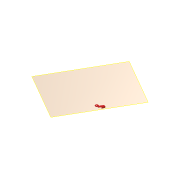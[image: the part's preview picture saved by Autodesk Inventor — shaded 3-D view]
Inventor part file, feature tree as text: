
AUTODESK INVENTOR PART (.ipt)
format: ipt  version: 2016 (Build 200138000, 138)  size: 402,432 bytes
history: native  units: mm
features: sheet_metal_op x13, reference x9, sketch x8, other x6, fillet x5, extrude x2, projected_geometry x2, plane x1
ambient origin geometry x8: Origin, YZ Plane, XZ Plane, XY Plane, X Axis, Y Axis, Z Axis, Center Point
bodies: Solid1 (feature_tree)
feature tree (46):
  plane  "Work Plane1"
  sheet_metal_op  "Face1"
  extrude  "Extrusion1"  Depth=0.6mm
  fillet  "Fillet1"  Radius=1.0mm
  fillet  "Fillet2"  Radius=3.0mm
  fillet  "Fillet3"  Radius=15.0mm
  sheet_metal_op  "Flange1"
  sheet_metal_op  "Flange2"
  sheet_metal_op  "Flange3"
  extrude  "Extrusion2"  Depth=0.4mm TaperAngle=0.0deg
  fillet  "Fillet4"  Radius=8.0mm
  sheet_metal_op  "Flange4"
  fillet  "Fillet5"  Radius=3.0mm
  sketch  "Sketch8"  dims[d19=0.2mm d20=0.8mm d21=0.6mm d22=4.0mm d23=20.071286mm d24=0.6mm d25=1.6mm d26=0.4mm d27=0.6mm d28=0.4mm d29=0.2mm d30=0.8mm d31=0.6mm d32=3.6mm d33=6.981317mm d34=0.6mm d35=1.6mm d36=0.4mm d37=0.6mm d38=0.4mm d39=0.2mm d40=0.8mm d41=0.6mm d42=7.8mm d43=22.078415mm d44=0.6mm d45=1.6mm d46=0.4mm d47=0.6mm d48=0.5mm d49=0.0mm d50=4.0mm d51=2.0mm d52=0.4mm d53=0.2mm d54=0.8mm d55=0.6mm d56=2.8mm d57=12.217305mm d58=0.6mm d59=1.6mm d60=0.4mm d61=0.6mm d64=4.3mm d65=6.25mm d1=10.0mm d2=4.7mm d6=1.0mm]
  sketch  "Sketch1"  dims[d0=16.0mm d3=0.6mm d4=1.0mm d5=3.0mm d7=15.0mm]
  reference  "Reference9"
  reference  "Reference10"
  reference  "Reference11"
  reference  "Reference12"
  reference  "Reference13"
  reference  "Reference14"
  reference  "Reference15"
  reference  "Reference16"
  other  "Plate1"
  sketch  "Sketch2"  dims[d8=2.0mm d9=1.0mm d10=0.4mm d11=0.0mm d12=8.0mm d13=3.0mm]
  projected_geometry  "Projected Loop1"
  reference  "Reference17"
  sketch  "Sketch3"  dims[d14=1.0mm]
  other  "Plate2"
  sheet_metal_op  "Bend1"
  sheet_metal_op  "Corner1"
  sketch  "Sketch4"  dims[d15=2.0mm]
  other  "Plate3"
  sheet_metal_op  "Bend2"
  sheet_metal_op  "Corner2"
  sketch  "Sketch5"  dims[d16=7.0mm]
  other  "Plate4"
  sheet_metal_op  "Bend3"
  sheet_metal_op  "Corner3"
  sketch  "Sketch6"  dims[d17=21.0mm]
  projected_geometry  "Projected Loop2"
  sketch  "Sketch7"  dims[d18=0.4mm]
  other  "Plate5"
  sheet_metal_op  "Bend4"
  sheet_metal_op  "Corner4"
  other  "Definition1"
